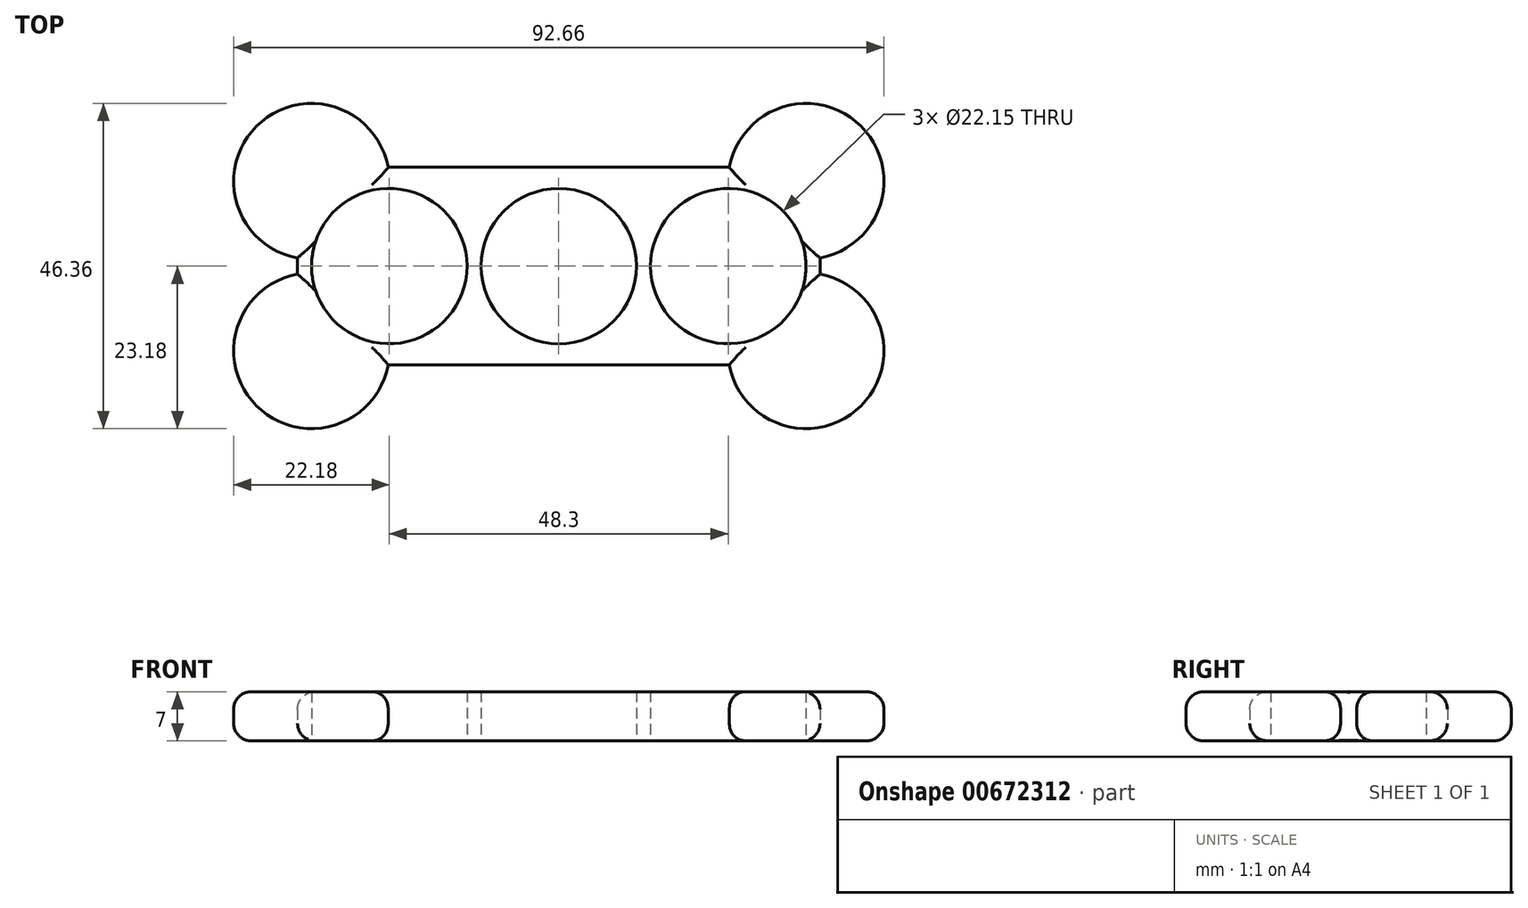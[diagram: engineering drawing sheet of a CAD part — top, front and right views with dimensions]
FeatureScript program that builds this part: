
annotation { "Feature Type Name" : "Feature", "Feature Type Description" : "" }
export const myFeature = defineFeature(function(context is Context, id is Id, definition is map)
    precondition{}
    {
        {
            var Q0;
            Q0=qCreatedBy(makeId("Top.planeOp"),FACE);
            var sketch = newSketch(context, id + "F0", { "sketchPlane" : qUnion([Q0])});
            skCircle(sketch, "E0", {"center": v(0, 0) * mm, "radius": 11.07 * mm});
            skCircle(sketch, "E1", {"center": v(24.15, 0) * mm, "radius": 11.07 * mm});
            skCircle(sketch, "E2", {"center": v(-24.15, 0) * mm, "radius": 11.07 * mm});
            skLineSegment(sketch, "E3.bottom", {"start": v(37.22, -14.08) * mm, "end": v(-37.22, -14.08) * mm});
            skLineSegment(sketch, "E3.top", {"start": v(37.22, 14.08) * mm, "end": v(-37.22, 14.08) * mm});
            skLineSegment(sketch, "E3.left", {"start": v(37.23, -14.08) * mm, "end": v(37.23, 14.08) * mm});
            skLineSegment(sketch, "E3.right", {"start": v(-37.23, -14.08) * mm, "end": v(-37.23, 14.08) * mm});
            skCircle(sketch, "E4", {"center": v(-35.23, -12.08) * mm, "radius": 11.1 * mm});
            skCircle(sketch, "E5", {"center": v(35.23, 12.08) * mm, "radius": 11.1 * mm});
            skCircle(sketch, "E6", {"center": v(35.23, -12.08) * mm, "radius": 11.1 * mm});
            skCircle(sketch, "E7", {"center": v(-35.23, 12.08) * mm, "radius": 11.1 * mm});
            skSolve(sketch);
        }
        {
            var Q0;
            Q0 = qSketchRegion(id + "F0", true);
            extrude(context, id + "F1", {"entities" : qUnion([Q0]), "depth" : 7 * mm, "offsetDistance" : 25 * mm});
        }
        {
            var Q0;
            Q0=makeQuery(id+"F1.opExtrude","CAP_EDGE",EDGE,{"disambiguationData":[OSD([sQuery(id+"F0.wireOp",EDGE,"E4")])],"isStart":true});
            var Q1;
            Q1=makeQuery(id+"F1.opExtrude","CAP_EDGE",EDGE,{"disambiguationData":[OSD([sQuery(id+"F0.wireOp",EDGE,"E7")])],"isStart":true});
            var Q2;
            Q2=makeQuery(id+"F1.opExtrude","CAP_EDGE",EDGE,{"disambiguationData":[OSD([sQuery(id+"F0.wireOp",EDGE,"E3.right")])],"isStart":true});
            var Q3;
            Q3=makeQuery(id+"F1.opExtrude","CAP_EDGE",EDGE,{"disambiguationData":[OSD([sQuery(id+"F0.wireOp",EDGE,"E3.top")])],"isStart":true});
            var Q4;
            Q4=makeQuery(id+"F1.opExtrude","CAP_EDGE",EDGE,{"disambiguationData":[OSD([sQuery(id+"F0.wireOp",EDGE,"E3.bottom")])],"isStart":true});
            var Q5;
            Q5=makeQuery(id+"F1.opExtrude","CAP_EDGE",EDGE,{"disambiguationData":[OSD([sQuery(id+"F0.wireOp",EDGE,"E6")])],"isStart":true});
            var Q6;
            Q6=makeQuery(id+"F1.opExtrude","CAP_EDGE",EDGE,{"disambiguationData":[OSD([sQuery(id+"F0.wireOp",EDGE,"E3.left")])],"isStart":true});
            var Q7;
            Q7=makeQuery(id+"F1.opExtrude","CAP_EDGE",EDGE,{"disambiguationData":[OSD([sQuery(id+"F0.wireOp",EDGE,"E5")])],"isStart":true});
            var Q8;
            Q8=makeQuery(id+"F1.opExtrude","CAP_EDGE",EDGE,{"disambiguationData":[OSD([sQuery(id+"F0.wireOp",EDGE,"E7")])],"isStart":false});
            var Q9;
            Q9=makeQuery(id+"F1.opExtrude","CAP_EDGE",EDGE,{"disambiguationData":[OSD([sQuery(id+"F0.wireOp",EDGE,"E4")])],"isStart":false});
            var Q10;
            Q10=makeQuery(id+"F1.opExtrude","CAP_EDGE",EDGE,{"disambiguationData":[OSD([sQuery(id+"F0.wireOp",EDGE,"E3.bottom")])],"isStart":false});
            var Q11;
            Q11=makeQuery(id+"F1.opExtrude","CAP_EDGE",EDGE,{"disambiguationData":[OSD([sQuery(id+"F0.wireOp",EDGE,"E3.top")])],"isStart":false});
            var Q12;
            Q12=makeQuery(id+"F1.opExtrude","CAP_EDGE",EDGE,{"disambiguationData":[OSD([sQuery(id+"F0.wireOp",EDGE,"E5")])],"isStart":false});
            var Q13;
            Q13=makeQuery(id+"F1.opExtrude","CAP_EDGE",EDGE,{"disambiguationData":[OSD([sQuery(id+"F0.wireOp",EDGE,"E6")])],"isStart":false});
            var Q14;
            Q14=makeQuery(id+"F1.opExtrude","CAP_EDGE",EDGE,{"disambiguationData":[OSD([sQuery(id+"F0.wireOp",EDGE,"E3.left")])],"isStart":false});
            var Q15;
            Q15=makeQuery(id+"F1.opExtrude","CAP_EDGE",EDGE,{"disambiguationData":[OSD([sQuery(id+"F0.wireOp",EDGE,"E3.right")])],"isStart":false});
            fillet(context, id + "F2", {"entities" : qUnion([Q0, Q1, Q2, Q3, Q4, Q5, Q6, Q7, Q8, Q9, Q10, Q11, Q12, Q13, Q14, Q15]), "radius" : 2.5 * mm, "tangentPropagation" : true, "allowEdgeOverflow" : false});
        }
    });
